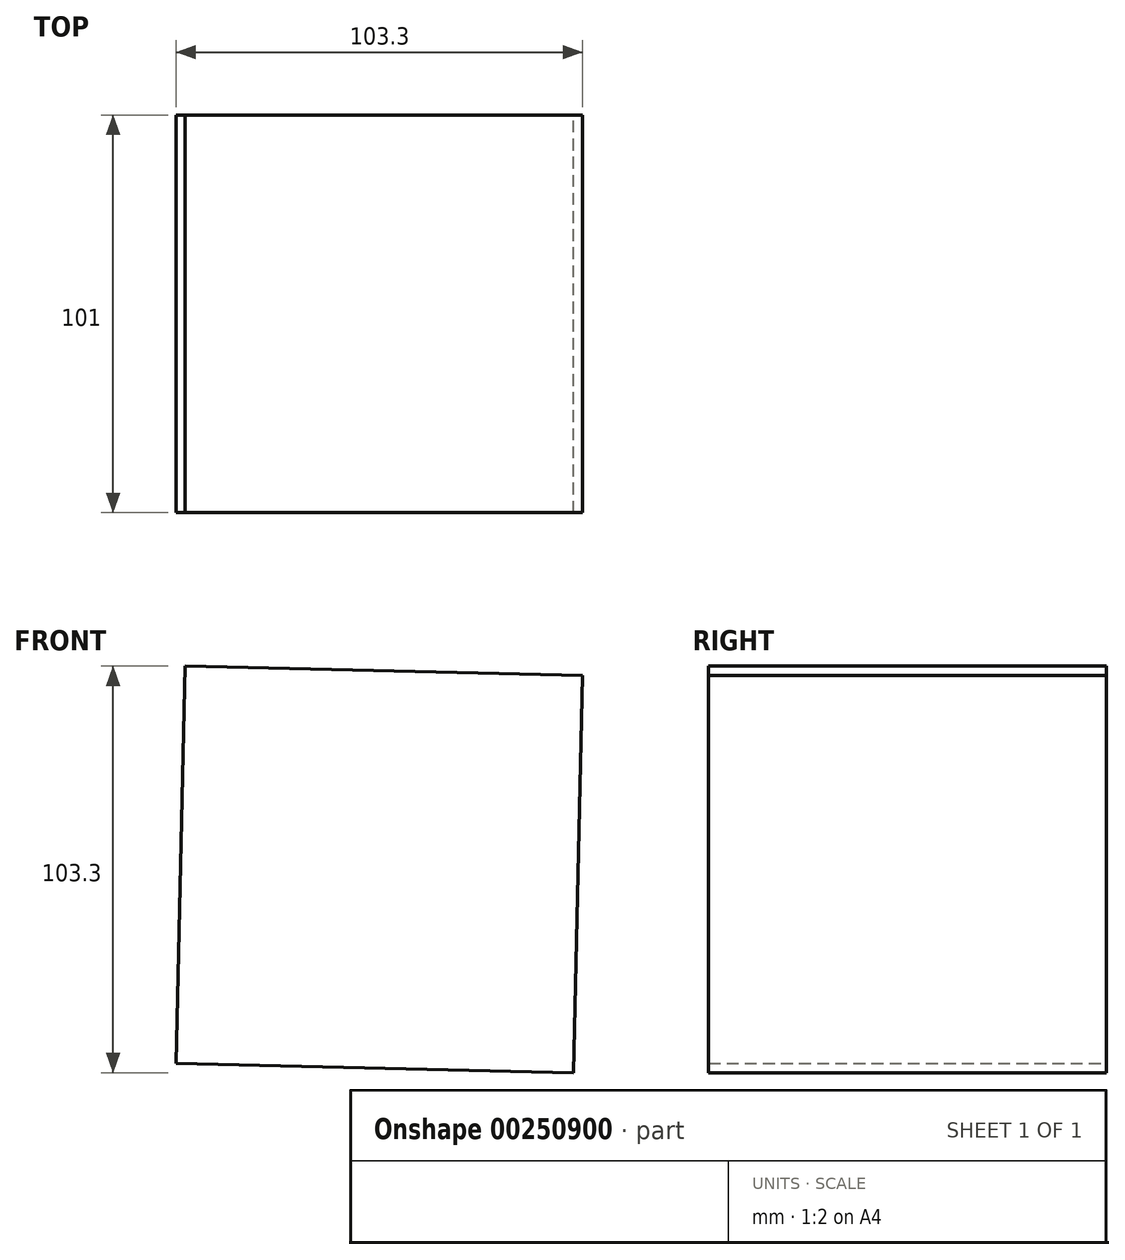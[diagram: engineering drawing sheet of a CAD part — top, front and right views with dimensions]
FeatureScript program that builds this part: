
annotation { "Feature Type Name" : "Feature", "Feature Type Description" : "" }
export const myFeature = defineFeature(function(context is Context, id is Id, definition is map)
    precondition{}
    {
        {
            var Q0;
            Q0=qCreatedBy(makeId("Front.planeOp"),FACE);
            var sketch = newSketch(context, id + "F0", { "sketchPlane" : qUnion([Q0])});
            skCircle(sketch, "E0.cCircle", {"center": v(0, 0) * mm, "radius": 71.42 * mm, "construction": true});
            skLineSegment(sketch, "E0.0", {"start": v(49.33, -51.65) * mm, "end": v(-51.65, -49.33) * mm});
            skLineSegment(sketch, "E0.1", {"start": v(-51.65, -49.33) * mm, "end": v(-49.33, 51.65) * mm});
            skLineSegment(sketch, "E0.2", {"start": v(-49.33, 51.65) * mm, "end": v(51.65, 49.33) * mm});
            skLineSegment(sketch, "E0.3", {"start": v(51.65, 49.33) * mm, "end": v(49.33, -51.65) * mm});
            skSolve(sketch);
        }
        {
            var Q0;
            Q0=makeQuery(id+"F0.imprint","IMPRINT",FACE,{"disambiguationData":[TD([[makeQuery(id+"F0.imprint","IMPRINT",EDGE,{"derivedFrom":sQuery(id+"F0.wireOp",EDGE,"E0.0")}),-1.0]])]});
            extrude(context, id + "F1", {"entities" : qUnion([Q0]), "endBound" : BoundingType.SYMMETRIC, "depth" : 101 * mm});
        }
    });
